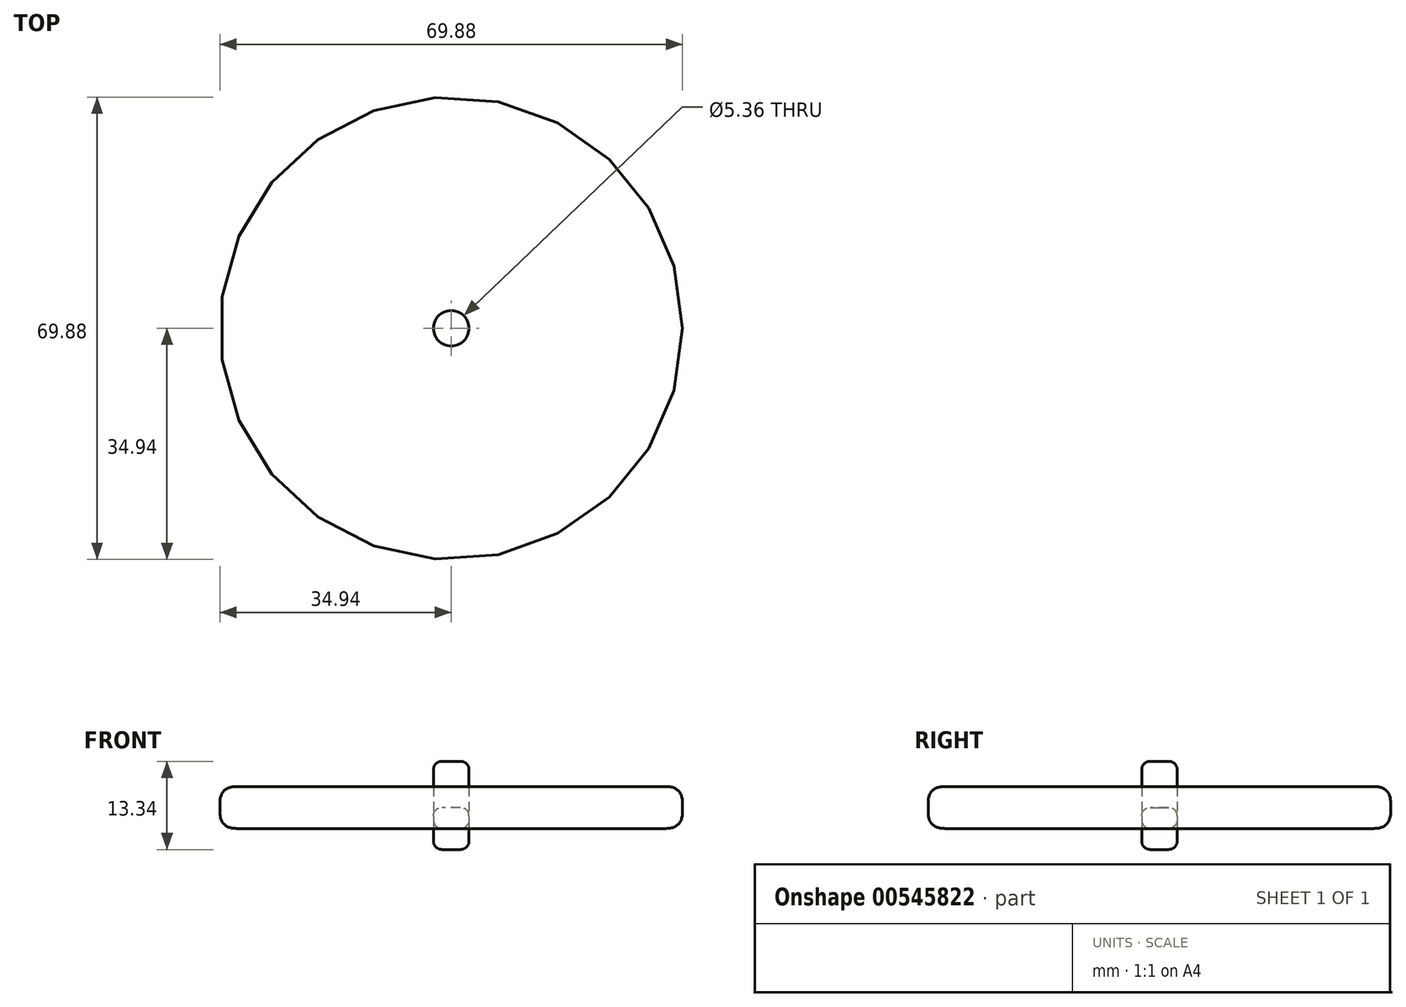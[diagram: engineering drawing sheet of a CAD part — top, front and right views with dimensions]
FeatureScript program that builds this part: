
annotation { "Feature Type Name" : "Feature", "Feature Type Description" : "" }
export const myFeature = defineFeature(function(context is Context, id is Id, definition is map)
    precondition{}
    {
        {
            var Q0;
            Q0=qCreatedBy(makeId("Top.planeOp"),FACE);
            var sketch = newSketch(context, id + "F0", { "sketchPlane" : qUnion([Q0])});
            skCircle(sketch, "E0", {"center": v(0, 0) * mm, "radius": 34.94 * mm});
            skCircle(sketch, "E1", {"center": v(0, 0) * mm, "radius": 2.68 * mm});
            skSolve(sketch);
        }
        {
            var Q0;
            Q0=makeQuery(id+"F0.imprint","IMPRINT",FACE,{"disambiguationData":[TD([[makeQuery(id+"F0.imprint","IMPRINT",EDGE,{"derivedFrom":sQuery(id+"F0.wireOp",EDGE,"E0")}),1.0]])]});
            var Q1;
            Q1=sQuery(id+"F0.wireOp",EDGE,"E0");
            extrude(context, id + "F1", {"entities" : qUnion([Q0]), "surfaceEntities" : qUnion([Q1]), "depth" : 6.35 * mm, "offsetDistance" : 25.4 * mm});
        }
        {
            var Q0;
            Q0=makeQuery(id+"F1.opExtrude","SWEPT_FACE",FACE,{"disambiguationData":[OSD([sQuery(id+"F0.wireOp",EDGE,"E0")])]});
            fillet(context, id + "F2", {"entities" : qUnion([Q0]), "radius" : 2.54 * mm, "tangentPropagation" : true, "rho" : 0.5, "crossSection" : FilletCrossSection.CONIC, "allowEdgeOverflow" : false});
        }
        {
            var Q0;
            Q0=makeQuery(id+"F0.imprint","IMPRINT",FACE,{"disambiguationData":[TD([[makeQuery(id+"F0.imprint","IMPRINT",EDGE,{"derivedFrom":sQuery(id+"F0.wireOp",EDGE,"E1")}),1.0]])]});
            extrude(context, id + "F3", {"entities" : qUnion([Q0]), "depth" : 10.16 * mm, "offsetDistance" : 25.4 * mm});
        }
        {
            var Q0;
            Q0=makeQuery(id+"F0.imprint","IMPRINT",FACE,{"disambiguationData":[TD([[makeQuery(id+"F0.imprint","IMPRINT",EDGE,{"derivedFrom":sQuery(id+"F0.wireOp",EDGE,"E1")}),1.0]])]});
            extrude(context, id + "F4", {"entities" : qUnion([Q0]), "endBound" : BoundingType.SYMMETRIC, "depth" : 6.35 * mm, "offsetDistance" : 25.4 * mm});
        }
        {
            var Q0;
            Q0=makeQuery(id+"F3.opExtrude","SWEPT_FACE",FACE,{"disambiguationData":[OSD([sQuery(id+"F0.wireOp",EDGE,"E1")])]});
            var Q1;
            Q1=makeQuery(id+"F4.opExtrude","SWEPT_FACE",FACE,{"disambiguationData":[OSD([sQuery(id+"F0.wireOp",EDGE,"E1")])]});
            fillet(context, id + "F5", {"entities" : qUnion([Q0, Q1]), "radius" : 1.27 * mm, "tangentPropagation" : true, "allowEdgeOverflow" : false});
        }
    });
